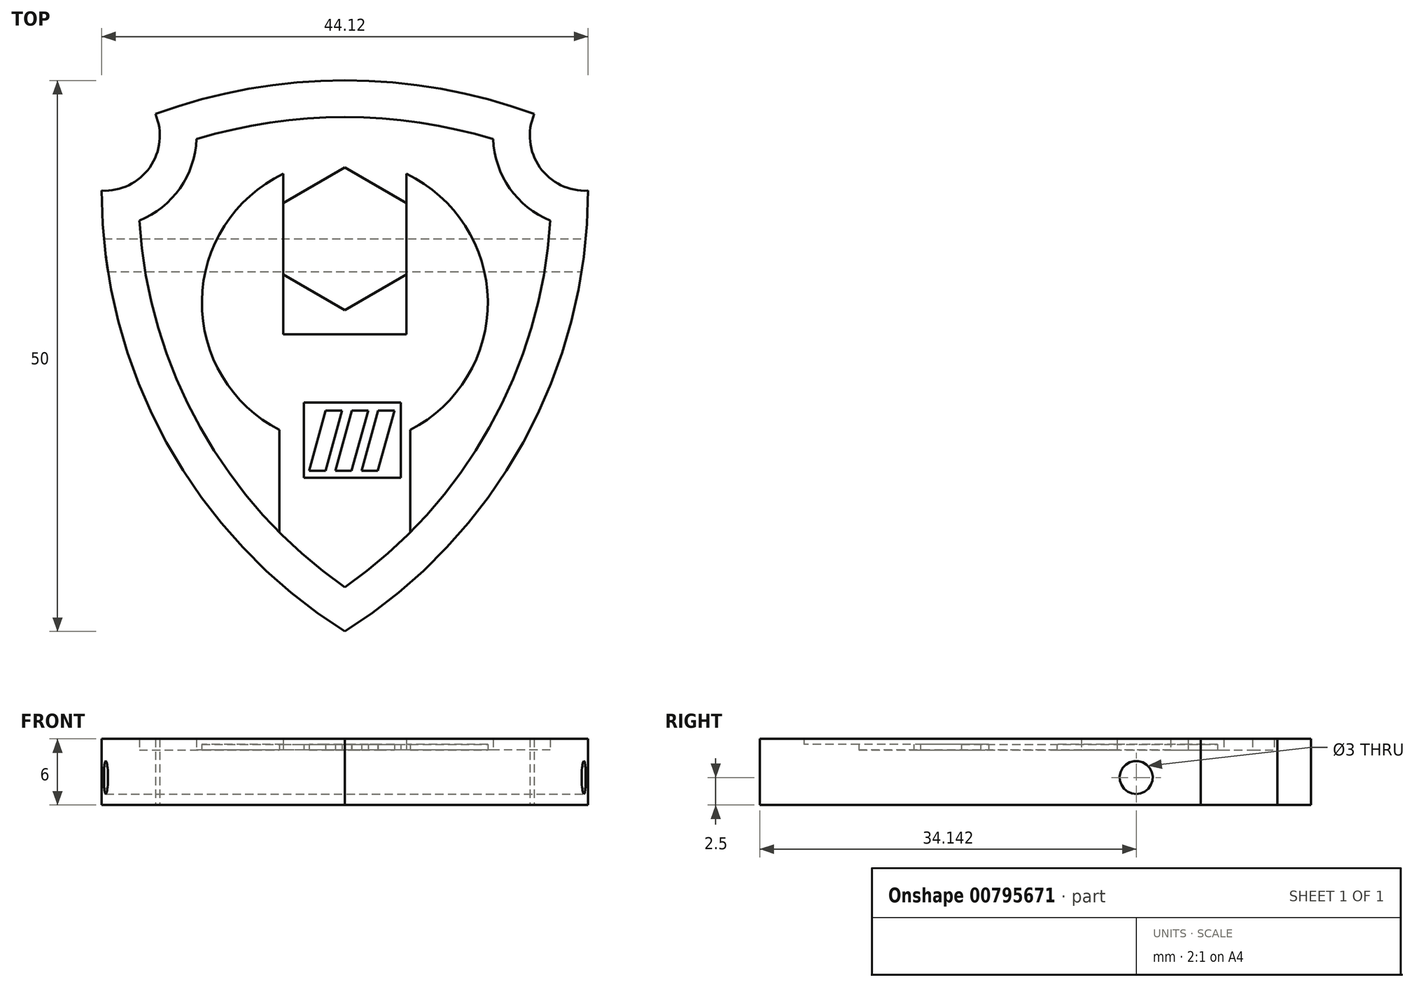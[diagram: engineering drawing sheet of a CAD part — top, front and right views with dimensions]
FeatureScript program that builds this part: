
annotation { "Feature Type Name" : "Feature", "Feature Type Description" : "" }
export const myFeature = defineFeature(function(context is Context, id is Id, definition is map)
    precondition{}
    {
        {
            assignVariable(context, id + "F0", {"name" : "thickness", "lengthValue" : 6 * mm, "variableType" : VariableType.LENGTH});
        }
        {
            assignVariable(context, id + "F1", {"name" : "emboss", "lengthValue" : 1 * mm, "variableType" : VariableType.LENGTH});
        }
        {
            var Q0;
            Q0=qCreatedBy(makeId("Top.planeOp"),FACE);
            var sketch = newSketch(context, id + "F2", { "sketchPlane" : qUnion([Q0])});
            skArc(sketch, "E0", {"start": v(0, 25) * mm, "mid": v(-8.73, 24.23) * mm, "end": v(-17.18, 21.95) * mm});
            skArc(sketch, "E1", {"start": v(-21.8, 20) * mm, "mid": v(-22, 17.5) * mm, "end": v(-22.06, 15) * mm, "construction": true});
            skLineSegment(sketch, "E2", {"start": v(-48.8, 15) * mm, "end": v(49.97, 15) * mm, "construction": true});
            skLineSegment(sketch, "E3", {"start": v(-46.4, 20) * mm, "end": v(44.94, 20) * mm, "construction": true});
            skArc(sketch, "E4", {"start": v(-22.06, 15) * mm, "mid": v(-17.7, 17.13) * mm, "end": v(-17.18, 21.95) * mm});
            skLineSegment(sketch, "E5", {"start": v(-46, 25) * mm, "end": v(67.16, 25) * mm, "construction": true});
            skLineSegment(sketch, "E6", {"start": v(-56.37, -25) * mm, "end": v(70.66, -25) * mm, "construction": true});
            skLineSegment(sketch, "E7", {"start": v(0, 25) * mm, "end": v(0, -25) * mm});
            skArc(sketch, "E8", {"start": v(-17.18, 21.95) * mm, "mid": v(-19.51, 21.03) * mm, "end": v(-21.8, 20) * mm, "construction": true});
            skArc(sketch, "E9", {"start": v(-22.06, 15) * mm, "mid": v(-16.18, -7.84) * mm, "end": v(0, -25) * mm});
            skArc(sketch, "E10.0", {"start": v(-18.64, 12.28) * mm, "mid": v(-13.12, -6.49) * mm, "end": v(0, -21) * mm});
            skArc(sketch, "E10.1", {"start": v(-18.64, 12.28) * mm, "mid": v(-14.96, 15.22) * mm, "end": v(-13.46, 19.68) * mm});
            skArc(sketch, "E10.2", {"start": v(0, 21.67) * mm, "mid": v(-6.8, 21.17) * mm, "end": v(-13.46, 19.68) * mm});
            skSolve(sketch);
        }
        {
            var Q0;
            {var subQ3=sQuery(id+"F2.wireOp",EDGE,"E0");Q0=makeQuery(id+"F2.imprint","IMPRINT",FACE,{"disambiguationData":[TD([[makeQuery(id+"F2.imprint","IMPRINT",EDGE,{"derivedFrom":subQ3}),1.0]])]});}
            extrude(context, id + "F3", {"entities" : qUnion([Q0]), "depth" : getVariable(context, 'thickness'), "offsetDistance" : 25 * mm});
        }
        {
            var Q0;
            {var subQ0=sQuery(id+"F2.wireOp",EDGE,"E10.0");Q0=makeQuery(id+"F2.imprint","IMPRINT",FACE,{"disambiguationData":[TD([[makeQuery(id+"F2.imprint","IMPRINT",EDGE,{"derivedFrom":subQ0}),1.0]])]});}
            extrude(context, id + "F4", {"entities" : qUnion([Q0]), "operationType" : NewBodyOperationType.ADD, "depth" : getVariable(context, 'thickness') - getVariable(context, 'emboss'), "offsetDistance" : 25 * mm});
        }
        {
            var Q0;
            Q0=makeQuery(id+"F3.opExtrude","SWEPT_BODY",BODY,{"disambiguationData":[OSD([sQuery(id+"F2.wireOp",EDGE,"E0"),sQuery(id+"F2.wireOp",EDGE,"E4"),sQuery(id+"F2.wireOp",EDGE,"E7"),sQuery(id+"F2.wireOp",EDGE,"E9"),sQuery(id+"F2.wireOp",EDGE,"E10.0"),sQuery(id+"F2.wireOp",EDGE,"E10.1"),sQuery(id+"F2.wireOp",EDGE,"E10.2")])]});
            var Q1;
            Q1=qCreatedBy(makeId("Right.planeOp"),FACE);
            mirror(context, id + "F5", {"operationType" : NewBodyOperationType.ADD, "entities" : qUnion([Q0]), "mirrorPlane" : qUnion([Q1])});
        }
        {
            var Q0;
            Q0=qCreatedBy(makeId("Top.planeOp"),FACE);
            var sketch = newSketch(context, id + "F6", { "sketchPlane" : qUnion([Q0])});
            skEllipse(sketch, "E11", {"center": v(-2.4, 15.1) * mm, "majorRadius": 7.08 * mm, "minorRadius": 5.76 * mm, "majorAxis": v(-0.25, 0.97)});
            skEllipse(sketch, "E12", {"center": v(-13.85, 5.8) * mm, "majorRadius": 6.69 * mm, "minorRadius": 5.37 * mm, "majorAxis": v(-0.87, 0.5)});
            skEllipse(sketch, "E13", {"center": v(11.13, 10.18) * mm, "majorRadius": 6.8 * mm, "minorRadius": 5.43 * mm, "majorAxis": v(0.68, 0.74)});
            skFitSpline(sketch, "E14", {"points": [v(1.12, 5.8) * mm, v(8.27, 2.78) * mm, v(11.8, -2.26) * mm, v(12.94, -6.02) * mm, v(11.75, -9.41) * mm, v(9.97, -10.88) * mm, v(7.86, -11.66) * mm, v(5.52, -11.52) * mm, v(3, -11.8) * mm, v(0, -13.03) * mm, v(-2.82, -13.76) * mm, v(-6.2, -13.35) * mm, v(-8.32, -11.61) * mm, v(-9.42, -8.63) * mm, v(-9.42, -5.47) * mm, v(-8.18, -1.53) * mm, v(-6.4, 1.22) * mm, v(-3.73, 3.78) * mm, v(-1.67, 5.07) * mm, v(1.12, 5.8) * mm]});
            skSolve(sketch);
        }
        {
            var Q0;
            Q0=qCreatedBy(makeId("Top.planeOp"),FACE);
            var sketch = newSketch(context, id + "F7", { "sketchPlane" : qUnion([Q0])});
            skCircle(sketch, "E15.cCircle", {"center": v(0, 10.64) * mm, "radius": 5.6 * mm, "construction": true});
            skLineSegment(sketch, "E15.0", {"start": v(5.6, 13.87) * mm, "end": v(5.6, 7.4) * mm});
            skLineSegment(sketch, "E15.1", {"start": v(5.6, 7.4) * mm, "end": v(0, 4.17) * mm});
            skLineSegment(sketch, "E15.2", {"start": v(0, 4.17) * mm, "end": v(-5.6, 7.4) * mm});
            skLineSegment(sketch, "E15.3", {"start": v(-5.6, 7.4) * mm, "end": v(-5.6, 13.87) * mm});
            skLineSegment(sketch, "E15.4", {"start": v(-5.6, 13.87) * mm, "end": v(0, 17.1) * mm});
            skLineSegment(sketch, "E15.5", {"start": v(0, 17.1) * mm, "end": v(5.6, 13.87) * mm});
            skPoint(sketch, "E15.0.midPoint", {"position": v(5.6, 10.64) * mm});
            skArc(sketch, "E16", {"start": v(-5.6, 16.52) * mm, "mid": v(-12.97, 5) * mm, "end": v(-5.93, -6.72) * mm});
            skLineSegment(sketch, "E17.top", {"start": v(-5.6, 1.95) * mm, "end": v(5.6, 1.95) * mm});
            skLineSegment(sketch, "E17.left", {"start": v(-5.6, 16.52) * mm, "end": v(-5.6, 1.95) * mm});
            skLineSegment(sketch, "E17.right", {"start": v(5.6, 16.52) * mm, "end": v(5.6, 1.95) * mm});
            skLineSegment(sketch, "E18.left", {"start": v(-5.93, -6.72) * mm, "end": v(-5.93, -19.32) * mm});
            skLineSegment(sketch, "E18.right", {"start": v(5.93, -6.72) * mm, "end": v(5.93, -20.12) * mm});
            skArc(sketch, "E19.trimOffspring", {"start": v(5.93, -6.72) * mm, "mid": v(12.97, 5) * mm, "end": v(5.6, 16.52) * mm});
            skLineSegment(sketch, "E20.bottom", {"start": v(-3.72, -4.23) * mm, "end": v(5.08, -4.23) * mm});
            skLineSegment(sketch, "E20.top", {"start": v(-3.72, -11.04) * mm, "end": v(5.08, -11.04) * mm});
            skLineSegment(sketch, "E20.left", {"start": v(-3.72, -4.23) * mm, "end": v(-3.72, -11.04) * mm});
            skLineSegment(sketch, "E20.right", {"start": v(5.08, -4.23) * mm, "end": v(5.08, -11.04) * mm});
            skLineSegment(sketch, "E21", {"start": v(-3.25, -10.43) * mm, "end": v(-1.76, -10.43) * mm});
            skLineSegment(sketch, "E22", {"start": v(-1.76, -10.43) * mm, "end": v(-0.25, -4.96) * mm});
            skLineSegment(sketch, "E23", {"start": v(-0.25, -4.96) * mm, "end": v(-1.74, -4.96) * mm});
            skLineSegment(sketch, "E24", {"start": v(-1.74, -4.96) * mm, "end": v(-3.25, -10.43) * mm});
            skLineSegment(sketch, "E25.1.0.0", {"start": v(2.13, -4.96) * mm, "end": v(0.64, -4.96) * mm});
            skLineSegment(sketch, "E25.1.0.1", {"start": v(0.62, -10.43) * mm, "end": v(2.13, -4.96) * mm});
            skLineSegment(sketch, "E25.1.0.2", {"start": v(0.64, -4.96) * mm, "end": v(-0.87, -10.43) * mm});
            skLineSegment(sketch, "E25.1.0.3", {"start": v(-0.87, -10.43) * mm, "end": v(0.62, -10.43) * mm});
            skLineSegment(sketch, "E25.2.0.0", {"start": v(4.5, -4.96) * mm, "end": v(3.02, -4.96) * mm});
            skLineSegment(sketch, "E25.2.0.1", {"start": v(3, -10.43) * mm, "end": v(4.5, -4.96) * mm});
            skLineSegment(sketch, "E25.2.0.2", {"start": v(3.02, -4.96) * mm, "end": v(1.51, -10.43) * mm});
            skLineSegment(sketch, "E25.2.0.3", {"start": v(1.51, -10.43) * mm, "end": v(3, -10.43) * mm});
            skLineSegment(sketch, "E25.direction1", {"start": v(-3.25, -10.43) * mm, "end": v(-0.87, -10.43) * mm, "construction": true});
            skLineSegment(sketch, "E26", {"start": v(-5.93, -19.32) * mm, "end": v(0, -23.42) * mm});
            skLineSegment(sketch, "E27", {"start": v(0, -23.42) * mm, "end": v(5.93, -20.12) * mm});
            skLineSegment(sketch, "E28", {"start": v(0, 23.21) * mm, "end": v(0, -3.26) * mm, "construction": true});
            skSolve(sketch);
        }
        {
            var Q0;
            {var subQ7=sQuery(id+"F7.wireOp",EDGE,"E16");Q0=makeQuery(id+"F7.imprint","IMPRINT",FACE,{"disambiguationData":[TD([[makeQuery(id+"F7.imprint","IMPRINT",EDGE,{"derivedFrom":subQ7}),1.0]])]});}
            var Q1;
            Q1=makeQuery(id+"F7.imprint","IMPRINT",FACE,{"disambiguationData":[TD([[makeQuery(id+"F7.imprint","IMPRINT",EDGE,{"derivedFrom":sQuery(id+"F7.wireOp",EDGE,"E21")}),1.0]])]});
            var Q2;
            Q2=makeQuery(id+"F7.imprint","IMPRINT",FACE,{"disambiguationData":[TD([[makeQuery(id+"F7.imprint","IMPRINT",EDGE,{"derivedFrom":sQuery(id+"F7.wireOp",EDGE,"E25.1.0.0")}),1.0]])]});
            var Q3;
            Q3=makeQuery(id+"F7.imprint","IMPRINT",FACE,{"disambiguationData":[TD([[makeQuery(id+"F7.imprint","IMPRINT",EDGE,{"derivedFrom":sQuery(id+"F7.wireOp",EDGE,"E25.2.0.0")}),1.0]])]});
            extrude(context, id + "F8", {"entities" : qUnion([Q0, Q1, Q2, Q3]), "operationType" : NewBodyOperationType.ADD, "depth" : getVariable(context, 'thickness') - (getVariable(context, 'emboss') / 2), "offsetDistance" : 25 * mm});
        }
        {
            var Q0;
            {var subQ3=sQuery(id+"F7.wireOp",EDGE,"E15.1");Q0=makeQuery(id+"F7.imprint","IMPRINT",FACE,{"disambiguationData":[TD([[makeQuery(id+"F7.imprint","IMPRINT",EDGE,{"derivedFrom":subQ3}),-1.0]])]});}
            extrude(context, id + "F9", {"entities" : qUnion([Q0]), "operationType" : NewBodyOperationType.ADD, "depth" : getVariable(context, 'thickness'), "offsetDistance" : 25 * mm});
        }
        {
            var Q0;
            Q0=qCreatedBy(makeId("Right.planeOp"),FACE);
            var sketch = newSketch(context, id + "F10", { "sketchPlane" : qUnion([Q0])});
            skCircle(sketch, "E29", {"center": v(9.14, 2.5) * mm, "radius": 1.5 * mm});
            skSolve(sketch);
        }
        {
            var Q0;
            Q0 = qSketchRegion(id + "F10", true);
            extrude(context, id + "F11", {"entities" : qUnion([Q0]), "operationType" : NewBodyOperationType.REMOVE, "endBound" : BoundingType.THROUGH_ALL, "oppositeDirection" : true, "depth" : 25 * mm, "offsetDistance" : 25 * mm, "hasSecondDirection" : true, "secondDirectionBound" : SecondDirectionBoundingType.THROUGH_ALL, "secondDirectionOppositeDirection" : false, "secondDirectionDepth" : 25 * mm});
        }
    });
